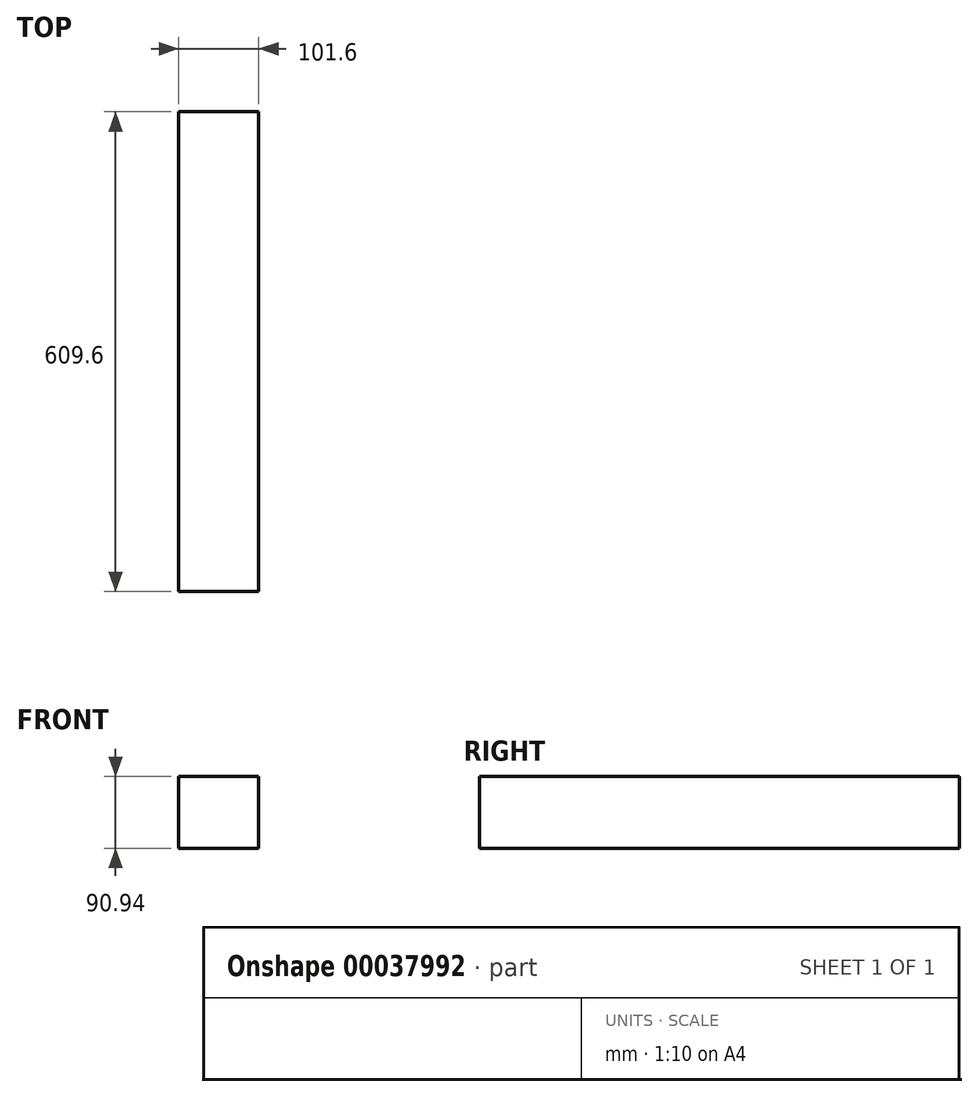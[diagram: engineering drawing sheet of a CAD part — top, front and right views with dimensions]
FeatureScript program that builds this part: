
annotation { "Feature Type Name" : "Feature", "Feature Type Description" : "" }
export const myFeature = defineFeature(function(context is Context, id is Id, definition is map)
    precondition{}
    {
        {
            var Q0;
            Q0=qCreatedBy(makeId("Top.planeOp"),FACE);
            var sketch = newSketch(context, id + "F0", { "sketchPlane" : qUnion([Q0])});
            skLineSegment(sketch, "E0.bottom", {"start": v(0, 0) * mm, "end": v(101.6, 0) * mm});
            skLineSegment(sketch, "E0.top", {"start": v(0, -609.6) * mm, "end": v(101.6, -609.6) * mm});
            skLineSegment(sketch, "E0.left", {"start": v(0, 0) * mm, "end": v(0, -609.6) * mm});
            skLineSegment(sketch, "E0.right", {"start": v(101.6, 0) * mm, "end": v(101.6, -609.6) * mm});
            skSolve(sketch);
        }
        {
            var Q0;
            Q0=qSketchRegion(id+"F0",true);
            extrude(context, id + "F1", {"entities" : qUnion([Q0]), "depth" : 90.94 * mm});
        }
    });
